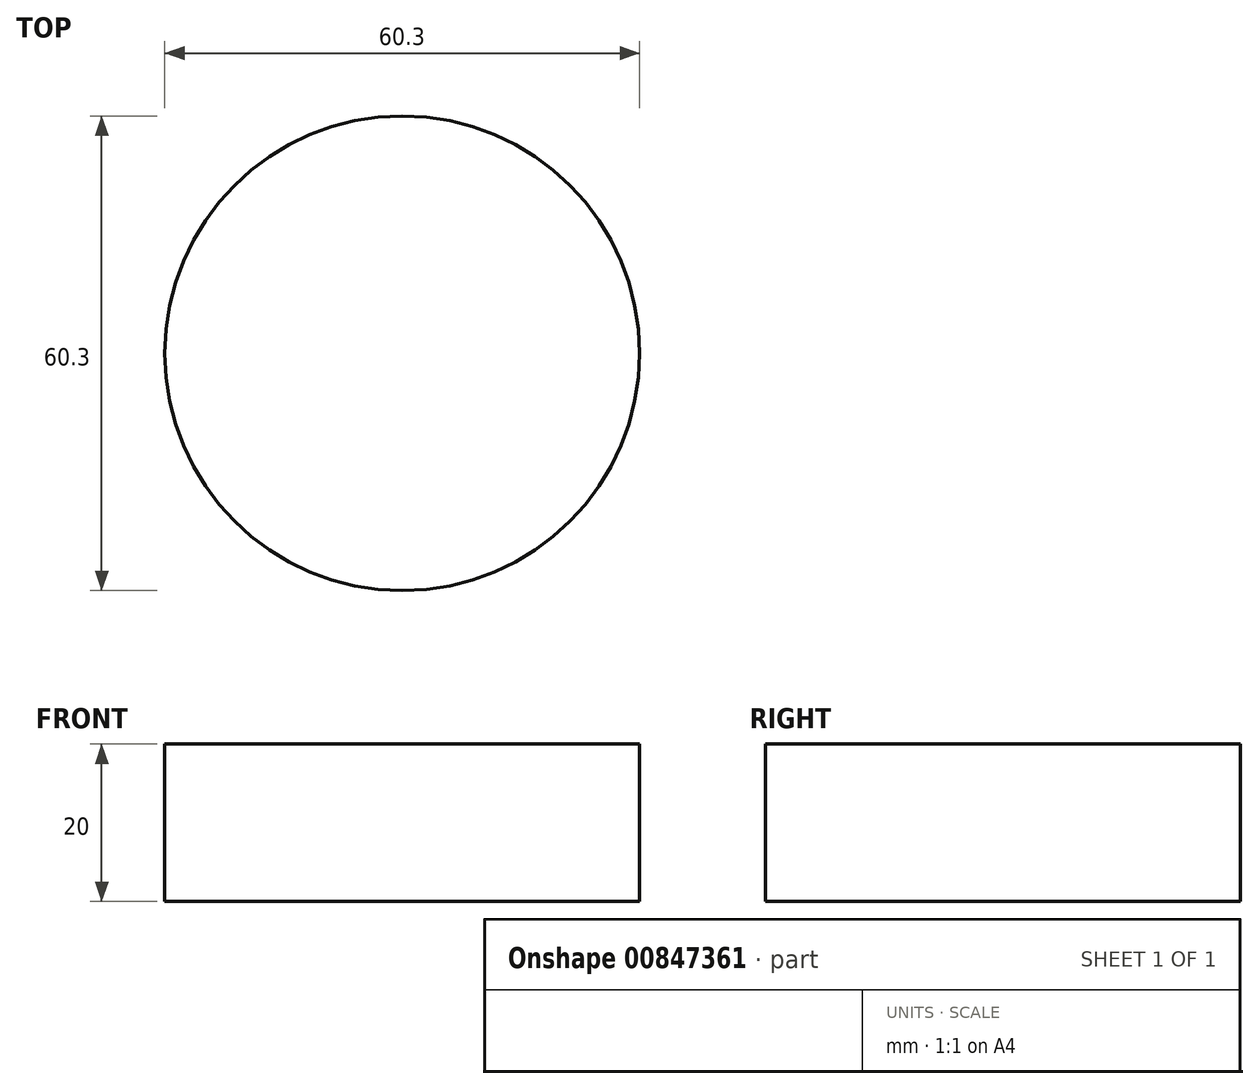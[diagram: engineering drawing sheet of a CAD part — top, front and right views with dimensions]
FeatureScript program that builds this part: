
annotation { "Feature Type Name" : "Feature", "Feature Type Description" : "" }
export const myFeature = defineFeature(function(context is Context, id is Id, definition is map)
    precondition{}
    {
        {
            var Q0;
            Q0=qCreatedBy(makeId("Top.planeOp"),FACE);
            var sketch = newSketch(context, id + "F0", { "sketchPlane" : qUnion([Q0])});
            skCircle(sketch, "E0", {"center": v(0, 0) * mm, "radius": 30.15 * mm});
            skSolve(sketch);
        }
        {
            var Q0;
            Q0=qSketchRegion(id+"F0",true);
            extrude(context, id + "F1", {"entities" : qUnion([Q0]), "depth" : 20 * mm, "offsetDistance" : 25 * mm});
        }
    });
